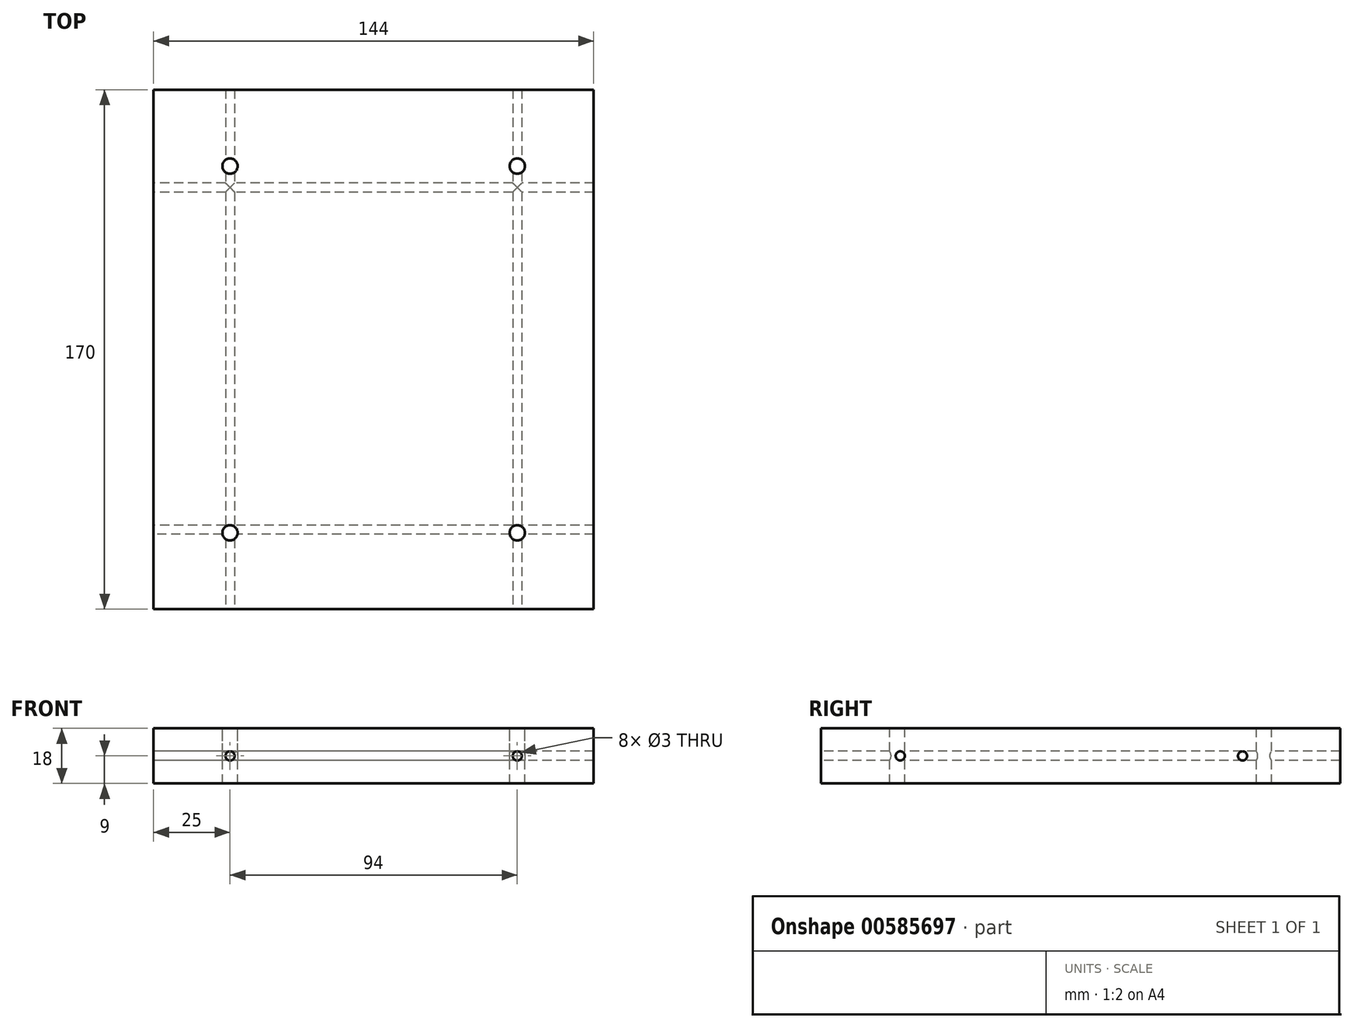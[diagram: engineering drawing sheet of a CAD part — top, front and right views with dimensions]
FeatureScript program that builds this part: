
annotation { "Feature Type Name" : "Feature", "Feature Type Description" : "" }
export const myFeature = defineFeature(function(context is Context, id is Id, definition is map)
    precondition{}
    {
        {
            var Q0;
            Q0=qCreatedBy(makeId("Top.planeOp"),FACE);
            var sketch = newSketch(context, id + "F0", { "sketchPlane" : qUnion([Q0])});
            skLineSegment(sketch, "E0.bottom", {"start": v(0, 0) * mm, "end": v(-144, 0) * mm});
            skLineSegment(sketch, "E0.top", {"start": v(0, -170) * mm, "end": v(-144, -170) * mm});
            skLineSegment(sketch, "E0.left", {"start": v(0, 0) * mm, "end": v(0, -170) * mm});
            skLineSegment(sketch, "E0.right", {"start": v(-144, 0) * mm, "end": v(-144, -170) * mm});
            skSolve(sketch);
        }
        {
            var Q0;
            Q0=makeQuery(id+"F0.imprint","IMPRINT",FACE,{"disambiguationData":[TD([[makeQuery(id+"F0.imprint","IMPRINT",EDGE,{"derivedFrom":sQuery(id+"F0.wireOp",EDGE,"E0.bottom")}),1.0]])]});
            extrude(context, id + "F1", {"entities" : qUnion([Q0]), "depth" : 18 * mm, "offsetDistance" : 25 * mm});
        }
        {
            var Q0;
            Q0=makeQuery(id+"F1.opExtrude","CAP_FACE",FACE,{"disambiguationData":[OSD([sQuery(id+"F0.wireOp",EDGE,"E0.bottom"),sQuery(id+"F0.wireOp",EDGE,"E0.top"),sQuery(id+"F0.wireOp",EDGE,"E0.left"),sQuery(id+"F0.wireOp",EDGE,"E0.right")])],"isStart":false});
            var sketch = newSketch(context, id + "F2", { "sketchPlane" : qUnion([Q0])});
            skCircle(sketch, "E1", {"center": v(-25, -145) * mm, "radius": 2.5 * mm});
            skCircle(sketch, "E2", {"center": v(-119, -145) * mm, "radius": 2.5 * mm});
            skCircle(sketch, "E3", {"center": v(-119, -25) * mm, "radius": 2.5 * mm});
            skCircle(sketch, "E4", {"center": v(-25, -25) * mm, "radius": 2.5 * mm});
            skSolve(sketch);
        }
        {
            var Q0;
            Q0 = qSketchRegion(id + "F2", true);
            extrude(context, id + "F3", {"entities" : qUnion([Q0]), "operationType" : NewBodyOperationType.REMOVE, "oppositeDirection" : true, "depth" : 18 * mm, "offsetDistance" : 25 * mm});
        }
        {
            var Q0;
            Q0=makeQuery(id+"F1.opExtrude","SWEPT_FACE",FACE,{"disambiguationData":[OSD([sQuery(id+"F0.wireOp",EDGE,"E0.top")])]});
            var sketch = newSketch(context, id + "F4", { "sketchPlane" : qUnion([Q0])});
            skCircle(sketch, "E5", {"center": v(-25, 9) * mm, "radius": 1.5 * mm});
            skCircle(sketch, "E6", {"center": v(-119, 9) * mm, "radius": 1.5 * mm});
            skSolve(sketch);
        }
        {
            var Q0;
            Q0 = qSketchRegion(id + "F4", true);
            extrude(context, id + "F5", {"entities" : qUnion([Q0]), "operationType" : NewBodyOperationType.REMOVE, "endBound" : BoundingType.THROUGH_ALL, "oppositeDirection" : true, "depth" : 25 * mm, "offsetDistance" : 25 * mm});
        }
        {
            var Q0;
            Q0=makeQuery(id+"F1.opExtrude","SWEPT_FACE",FACE,{"disambiguationData":[OSD([sQuery(id+"F0.wireOp",EDGE,"E0.right")])]});
            var sketch = newSketch(context, id + "F6", { "sketchPlane" : qUnion([Q0])});
            skCircle(sketch, "E7", {"center": v(32, 9) * mm, "radius": 1.5 * mm});
            skCircle(sketch, "E8", {"center": v(144, 9) * mm, "radius": 1.5 * mm});
            skSolve(sketch);
        }
        {
            var Q0;
            Q0 = qSketchRegion(id + "F6", true);
            extrude(context, id + "F7", {"entities" : qUnion([Q0]), "operationType" : NewBodyOperationType.REMOVE, "endBound" : BoundingType.THROUGH_ALL, "oppositeDirection" : true, "depth" : 25 * mm, "offsetDistance" : 25 * mm});
        }
    });
